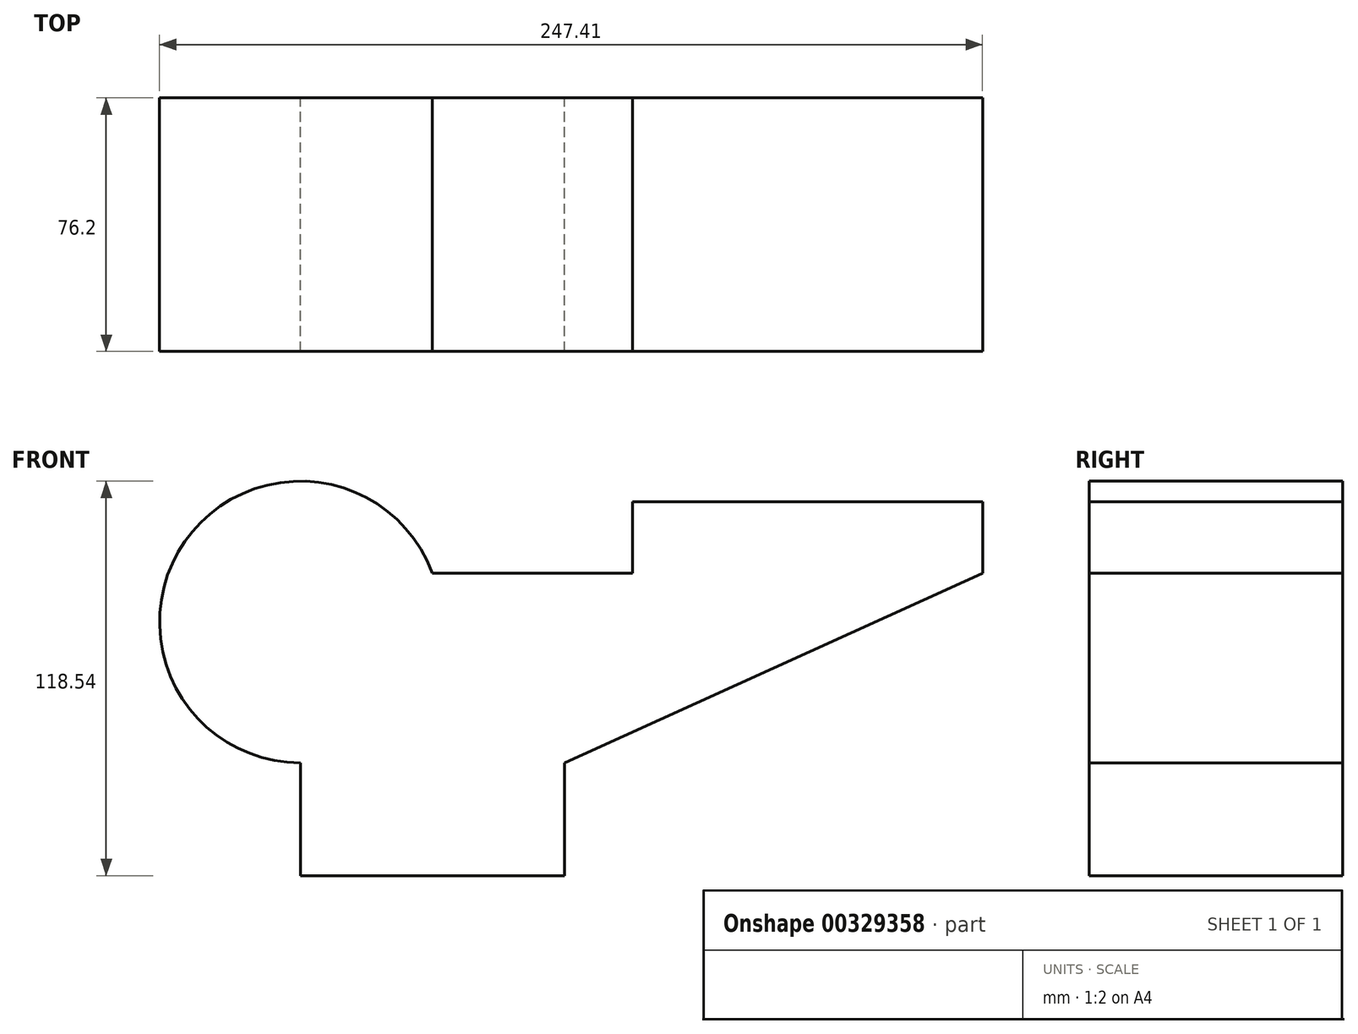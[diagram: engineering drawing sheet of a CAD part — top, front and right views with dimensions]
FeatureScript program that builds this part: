
annotation { "Feature Type Name" : "Feature", "Feature Type Description" : "" }
export const myFeature = defineFeature(function(context is Context, id is Id, definition is map)
    precondition{}
    {
        {
            var Q0;
            Q0=qCreatedBy(makeId("Front.planeOp"),FACE);
            var sketch = newSketch(context, id + "F0", { "sketchPlane" : qUnion([Q0])});
            skLineSegment(sketch, "E0.bottom", {"start": v(-39.68, 16.94) * mm, "end": v(39.68, 16.94) * mm});
            skLineSegment(sketch, "E0.top", {"start": v(-39.68, -16.94) * mm, "end": v(39.68, -16.94) * mm});
            skLineSegment(sketch, "E0.left", {"start": v(-39.68, 16.94) * mm, "end": v(-39.68, -16.94) * mm});
            skLineSegment(sketch, "E0.right", {"start": v(39.68, 16.94) * mm, "end": v(39.68, -16.94) * mm});
            skPoint(sketch, "E0.middle", {"position": v(0, 0) * mm});
            skLineSegment(sketch, "E1.bottom", {"start": v(165.4, 74) * mm, "end": v(60.19, 74) * mm});
            skLineSegment(sketch, "E1.top", {"start": v(165.4, 95.4) * mm, "end": v(60.19, 95.4) * mm});
            skLineSegment(sketch, "E1.left", {"start": v(165.4, 74) * mm, "end": v(165.4, 95.4) * mm});
            skLineSegment(sketch, "E1.right", {"start": v(60.19, 74) * mm, "end": v(60.19, 95.4) * mm});
            skPoint(sketch, "E1.middle", {"position": v(112.8, 84.7) * mm});
            skLineSegment(sketch, "E2", {"start": v(39.68, 16.94) * mm, "end": v(165.4, 74) * mm});
            skArc(sketch, "E3", {"start": v(-39.68, 16.94) * mm, "mid": v(-74.43, 83.43) * mm, "end": v(0, 74) * mm});
            skLineSegment(sketch, "E4", {"start": v(0, 74) * mm, "end": v(60.19, 74) * mm});
            skSolve(sketch);
        }
        {
            var Q0;
            Q0=makeQuery(id+"F0.imprint","IMPRINT",FACE,{"disambiguationData":[TD([[makeQuery(id+"F0.imprint","IMPRINT",EDGE,{"derivedFrom":sQuery(id+"F0.wireOp",EDGE,"E0.bottom")}),-1.0]])]});
            var Q1;
            Q1=makeQuery(id+"F0.imprint","IMPRINT",FACE,{"disambiguationData":[TD([[makeQuery(id+"F0.imprint","IMPRINT",EDGE,{"derivedFrom":sQuery(id+"F0.wireOp",EDGE,"E0.bottom")}),1.0]])]});
            var Q2;
            Q2=makeQuery(id+"F0.imprint","IMPRINT",FACE,{"disambiguationData":[TD([[makeQuery(id+"F0.imprint","IMPRINT",EDGE,{"derivedFrom":sQuery(id+"F0.wireOp",EDGE,"E1.bottom")}),-1.0]])]});
            extrude(context, id + "F1", {"entities" : qUnion([Q0, Q1, Q2]), "endBound" : BoundingType.SYMMETRIC, "depth" : 76.2 * mm});
        }
    });
